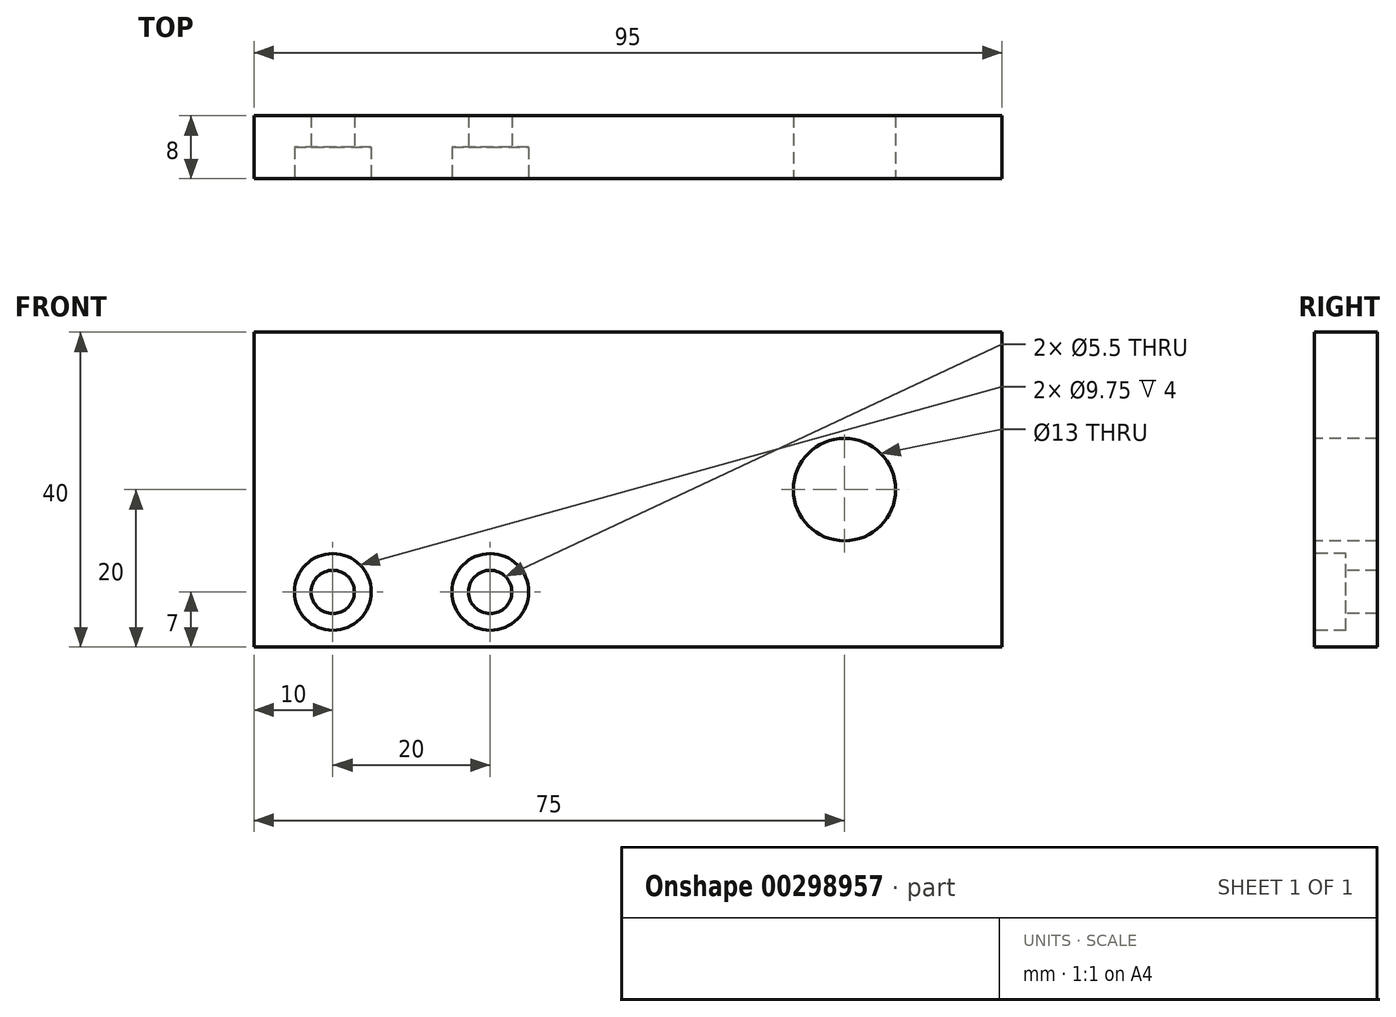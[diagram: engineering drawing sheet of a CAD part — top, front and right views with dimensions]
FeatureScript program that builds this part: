
annotation { "Feature Type Name" : "Feature", "Feature Type Description" : "" }
export const myFeature = defineFeature(function(context is Context, id is Id, definition is map)
    precondition{}
    {
        {
            var Q0;
            Q0=qCreatedBy(makeId("Front.planeOp"),FACE);
            var sketch = newSketch(context, id + "F0", { "sketchPlane" : qUnion([Q0])});
            skLineSegment(sketch, "E0.bottom", {"start": v(-47.5, 20) * mm, "end": v(47.5, 20) * mm});
            skLineSegment(sketch, "E0.top", {"start": v(-47.5, -20) * mm, "end": v(47.5, -20) * mm});
            skLineSegment(sketch, "E0.left", {"start": v(-47.5, 20) * mm, "end": v(-47.5, -20) * mm});
            skLineSegment(sketch, "E0.right", {"start": v(47.5, 20) * mm, "end": v(47.5, -20) * mm});
            skPoint(sketch, "E0.middle", {"position": v(0, 0) * mm});
            skPoint(sketch, "E1", {"position": v(-37.5, -13) * mm});
            skPoint(sketch, "E2", {"position": v(-17.5, -13) * mm});
            skPoint(sketch, "E3", {"position": v(27.5, 0) * mm});
            skSolve(sketch);
        }
        {
            var Q0;
            Q0=makeQuery(id+"F0.imprint","IMPRINT",FACE,{"disambiguationData":[TD([[makeQuery(id+"F0.imprint","IMPRINT",EDGE,{"derivedFrom":sQuery(id+"F0.wireOp",EDGE,"E0.bottom")}),-1.0]])]});
            extrude(context, id + "F1", {"entities" : qUnion([Q0]), "oppositeDirection" : true, "depth" : 8 * mm});
        }
        {
            var Q0;
            Q0=sQuery(id+"F0.wireOp",VERTEX,"E2");
            var Q1;
            Q1=sQuery(id+"F0.wireOp",VERTEX,"E1");
            var Q2;
            Q2=makeQuery(id+"F1.opExtrude","SWEPT_BODY",BODY,{"disambiguationData":[OSD([sQuery(id+"F0.wireOp",EDGE,"E0.bottom"),sQuery(id+"F0.wireOp",EDGE,"E0.top"),sQuery(id+"F0.wireOp",EDGE,"E0.left"),sQuery(id+"F0.wireOp",EDGE,"E0.right")])]});
            hole(context, id + "F2", {"style" : HoleStyle.C_BORE, "endStyle" : HoleEndStyle.THROUGH, "holeDiameter" : 5.5 * mm, "cBoreDiameter" : 9.75 * mm, "cBoreDepth" : 4 * mm, "isTappedThrough" : true, "tappedDepth" : 12 * mm, "tapClearance" : 3, "locations" : qUnion([Q0, Q1]), "scope" : qUnion([Q2])});
        }
        {
            var Q0;
            Q0=sQuery(id+"F0.wireOp",VERTEX,"E3");
            var Q1;
            Q1=makeQuery(id+"F1.opExtrude","SWEPT_BODY",BODY,{"disambiguationData":[OSD([sQuery(id+"F0.wireOp",EDGE,"E0.bottom"),sQuery(id+"F0.wireOp",EDGE,"E0.top"),sQuery(id+"F0.wireOp",EDGE,"E0.left"),sQuery(id+"F0.wireOp",EDGE,"E0.right")])]});
            hole(context, id + "F3", {"style" : HoleStyle.SIMPLE, "endStyle" : HoleEndStyle.THROUGH, "holeDiameter" : 13 * mm, "isTappedThrough" : true, "tappedDepth" : 12 * mm, "tapClearance" : 3, "locations" : qUnion([Q0]), "scope" : qUnion([Q1])});
        }
    });
